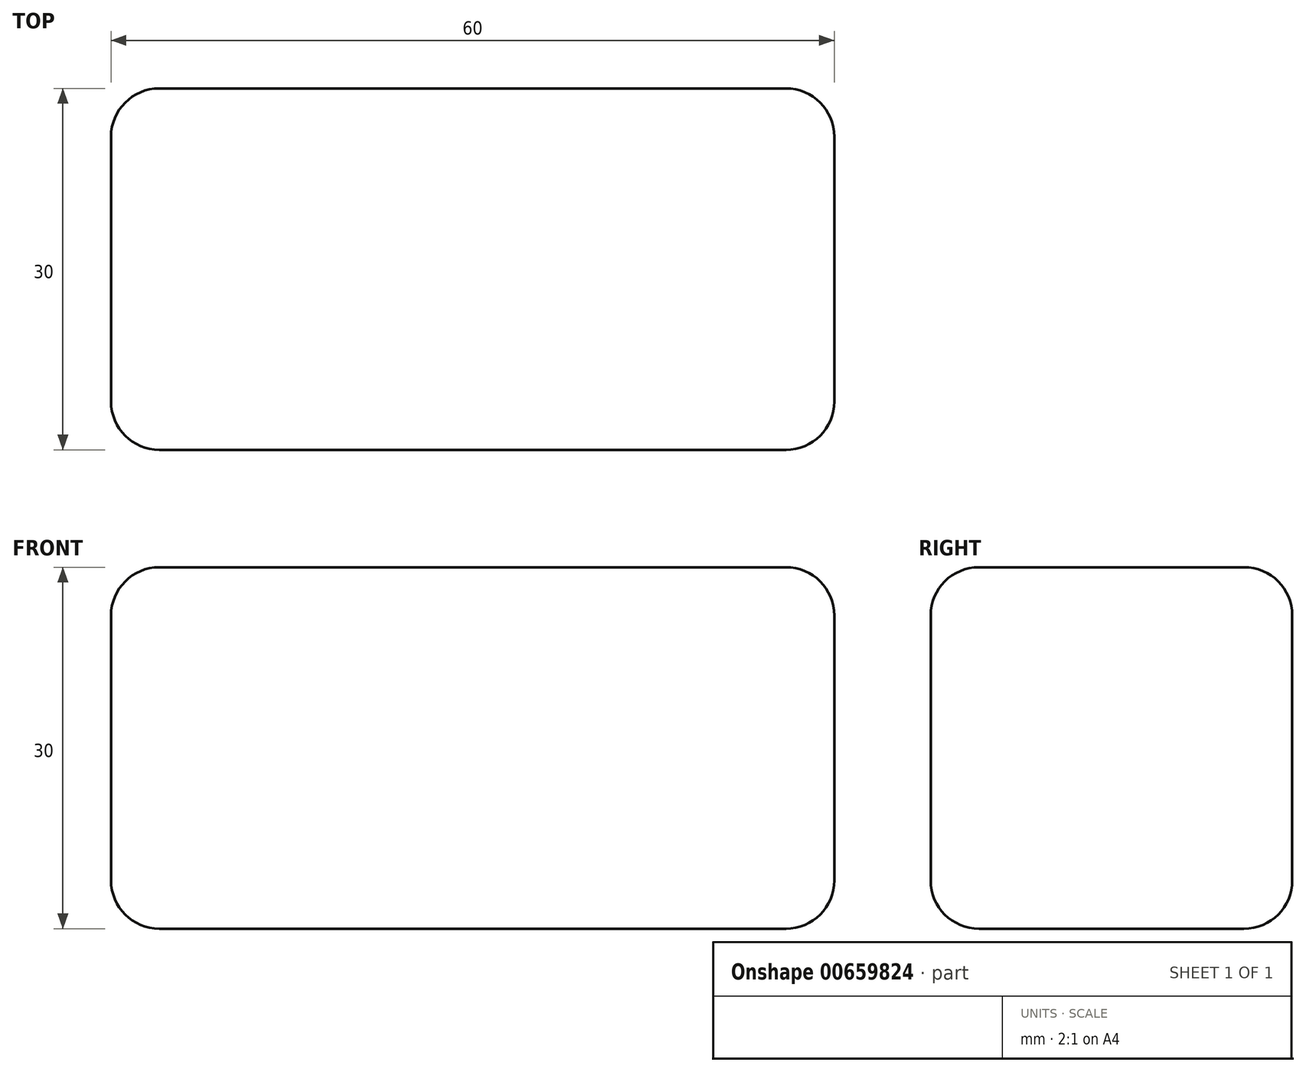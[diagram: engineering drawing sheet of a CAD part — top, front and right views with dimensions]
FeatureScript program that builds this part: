
annotation { "Feature Type Name" : "Feature", "Feature Type Description" : "" }
export const myFeature = defineFeature(function(context is Context, id is Id, definition is map)
    precondition{}
    {
        {
            var Q0;
            Q0=qCreatedBy(makeId("Top.planeOp"),FACE);
            var sketch = newSketch(context, id + "F0", { "sketchPlane" : qUnion([Q0])});
            skLineSegment(sketch, "E0.bottom", {"start": v(-30, 15) * mm, "end": v(30, 15) * mm});
            skLineSegment(sketch, "E0.top", {"start": v(-30, -15) * mm, "end": v(30, -15) * mm});
            skLineSegment(sketch, "E0.left", {"start": v(-30, 15) * mm, "end": v(-30, -15) * mm});
            skLineSegment(sketch, "E0.right", {"start": v(30, 15) * mm, "end": v(30, -15) * mm});
            skPoint(sketch, "E0.middle", {"position": v(0, 0) * mm});
            skSolve(sketch);
        }
        {
            var Q0;
            Q0 = qSketchRegion(id + "F0", true);
            extrude(context, id + "F1", {"entities" : qUnion([Q0]), "depth" : 30 * mm, "offsetDistance" : 25 * mm});
        }
        {
            var Q0;
            Q0=makeQuery(id+"F1.opExtrude","CAP_EDGE",EDGE,{"disambiguationData":[OSD([sQuery(id+"F0.wireOp",EDGE,"E0.top")])],"isStart":false});
            var Q1;
            Q1=makeQuery(id+"F1.opExtrude","CAP_EDGE",EDGE,{"disambiguationData":[OSD([sQuery(id+"F0.wireOp",EDGE,"E0.bottom")])],"isStart":false});
            var Q2;
            Q2=makeQuery(id+"F1.opExtrude","CAP_EDGE",EDGE,{"disambiguationData":[OSD([sQuery(id+"F0.wireOp",EDGE,"E0.left")])],"isStart":false});
            var Q3;
            Q3=makeQuery(id+"F1.opExtrude","CAP_EDGE",EDGE,{"disambiguationData":[OSD([sQuery(id+"F0.wireOp",EDGE,"E0.right")])],"isStart":false});
            var Q4;
            Q4=makeQuery(id+"F1.opExtrude","SWEPT_EDGE",EDGE,{"disambiguationData":[OSD([sQuery(id+"F0.wireOp",EDGE,"E0.top"),sQuery(id+"F0.wireOp",EDGE,"E0.right")])]});
            var Q5;
            Q5=makeQuery(id+"F1.opExtrude","SWEPT_EDGE",EDGE,{"disambiguationData":[OSD([sQuery(id+"F0.wireOp",EDGE,"E0.top"),sQuery(id+"F0.wireOp",EDGE,"E0.left")])]});
            var Q6;
            Q6=makeQuery(id+"F1.opExtrude","CAP_EDGE",EDGE,{"disambiguationData":[OSD([sQuery(id+"F0.wireOp",EDGE,"E0.top")])],"isStart":true});
            var Q7;
            Q7=makeQuery(id+"F1.opExtrude","CAP_EDGE",EDGE,{"disambiguationData":[OSD([sQuery(id+"F0.wireOp",EDGE,"E0.left")])],"isStart":true});
            var Q8;
            Q8=makeQuery(id+"F1.opExtrude","SWEPT_EDGE",EDGE,{"disambiguationData":[OSD([sQuery(id+"F0.wireOp",EDGE,"E0.bottom"),sQuery(id+"F0.wireOp",EDGE,"E0.left")])]});
            var Q9;
            Q9=makeQuery(id+"F1.opExtrude","CAP_EDGE",EDGE,{"disambiguationData":[OSD([sQuery(id+"F0.wireOp",EDGE,"E0.bottom")])],"isStart":true});
            var Q10;
            Q10=makeQuery(id+"F1.opExtrude","SWEPT_EDGE",EDGE,{"disambiguationData":[OSD([sQuery(id+"F0.wireOp",EDGE,"E0.bottom"),sQuery(id+"F0.wireOp",EDGE,"E0.right")])]});
            var Q11;
            Q11=makeQuery(id+"F1.opExtrude","CAP_EDGE",EDGE,{"disambiguationData":[OSD([sQuery(id+"F0.wireOp",EDGE,"E0.right")])],"isStart":true});
            fillet(context, id + "F2", {"entities" : qUnion([Q0, Q1, Q2, Q3, Q4, Q5, Q6, Q7, Q8, Q9, Q10, Q11]), "radius" : 4 * mm, "tangentPropagation" : true, "allowEdgeOverflow" : false});
        }
    });
